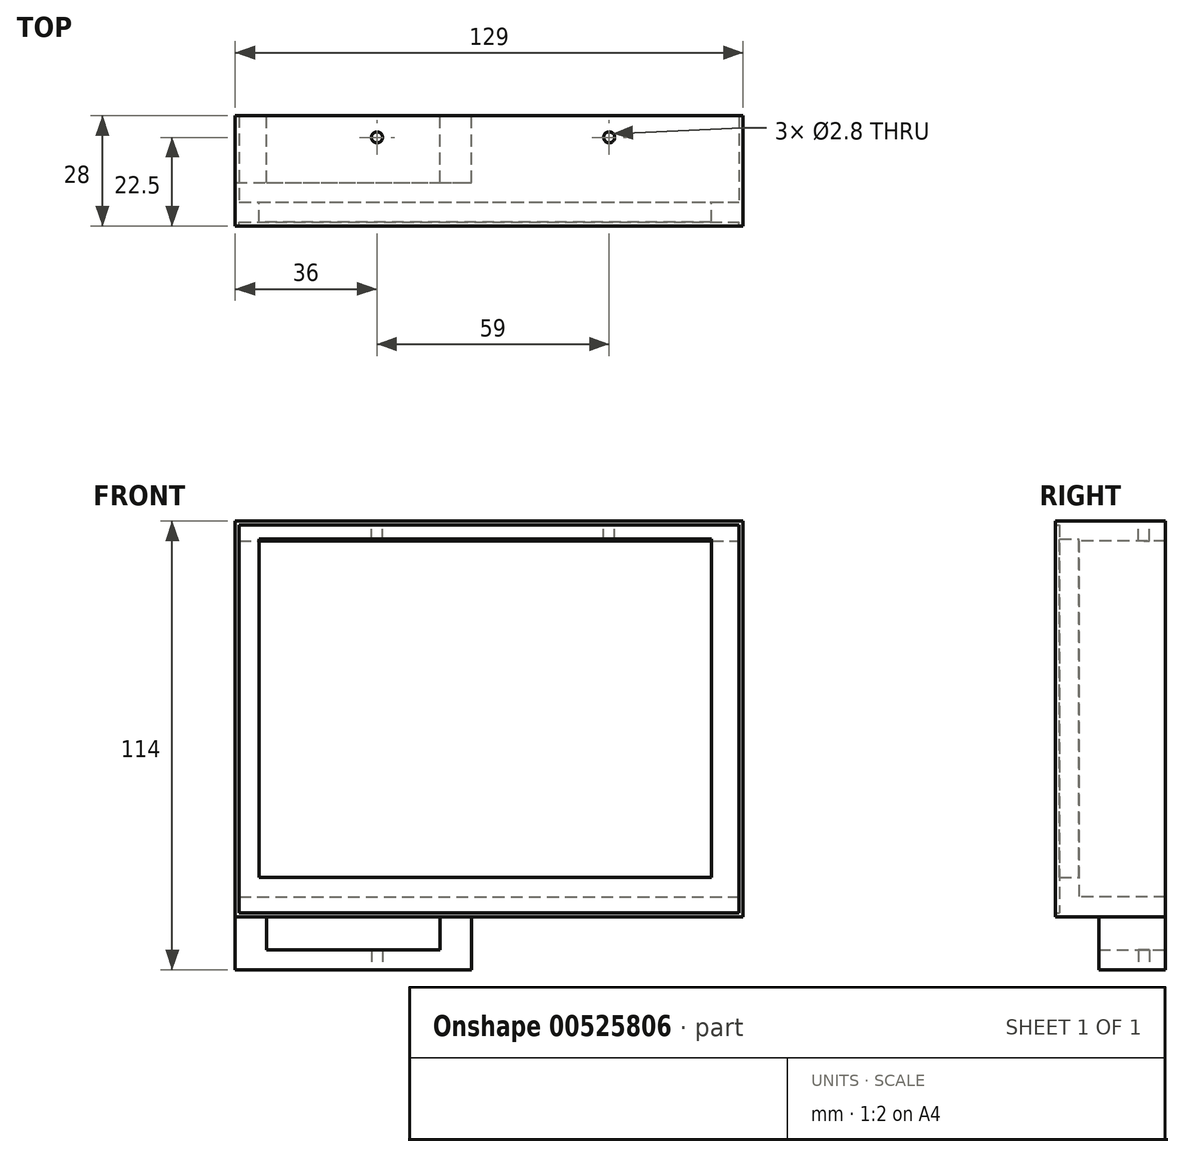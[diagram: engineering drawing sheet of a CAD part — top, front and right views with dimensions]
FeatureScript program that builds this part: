
annotation { "Feature Type Name" : "Feature", "Feature Type Description" : "" }
export const myFeature = defineFeature(function(context is Context, id is Id, definition is map)
    precondition{}
    {
        {
            var Q0;
            Q0=qCreatedBy(makeId("Front.planeOp"),FACE);
            var sketch = newSketch(context, id + "F0", { "sketchPlane" : qUnion([Q0])});
            skLineSegment(sketch, "E0.bottom", {"start": v(57.5, -43) * mm, "end": v(-57.5, -43) * mm});
            skLineSegment(sketch, "E0.top", {"start": v(57.5, 43) * mm, "end": v(-57.5, 43) * mm});
            skLineSegment(sketch, "E0.left", {"start": v(57.5, -43) * mm, "end": v(57.5, 43) * mm});
            skLineSegment(sketch, "E0.right", {"start": v(-57.5, -43) * mm, "end": v(-57.5, 43) * mm});
            skPoint(sketch, "E0.middle", {"position": v(0, 0) * mm});
            skLineSegment(sketch, "E1.bottom", {"start": v(-62.5, 46.5) * mm, "end": v(64.5, 46.5) * mm});
            skLineSegment(sketch, "E1.top", {"start": v(-62.5, -52) * mm, "end": v(64.5, -52) * mm});
            skLineSegment(sketch, "E1.left", {"start": v(-62.5, 46.5) * mm, "end": v(-62.5, -52) * mm});
            skLineSegment(sketch, "E1.right", {"start": v(64.5, 46.5) * mm, "end": v(64.5, -52) * mm});
            skSolve(sketch);
        }
        {
            var Q0;
            Q0=qCreatedBy(makeId("Front.planeOp"),FACE);
            var sketch = newSketch(context, id + "F1", { "sketchPlane" : qUnion([Q0])});
            skLineSegment(sketch, "E2.bottom", {"start": v(-62.5, 46.5) * mm, "end": v(64.5, 46.5) * mm});
            skLineSegment(sketch, "E2.top", {"start": v(-62.5, -52) * mm, "end": v(64.5, -52) * mm});
            skLineSegment(sketch, "E2.left", {"start": v(-62.5, 46.5) * mm, "end": v(-62.5, -52) * mm});
            skLineSegment(sketch, "E2.right", {"start": v(64.5, 46.5) * mm, "end": v(64.5, -52) * mm});
            skLineSegment(sketch, "E3.bottom", {"start": v(-63.5, 47.5) * mm, "end": v(65.5, 47.5) * mm});
            skLineSegment(sketch, "E3.top", {"start": v(-63.5, -53) * mm, "end": v(65.5, -53) * mm});
            skLineSegment(sketch, "E3.left", {"start": v(-63.5, 47.5) * mm, "end": v(-63.5, -53) * mm});
            skLineSegment(sketch, "E3.right", {"start": v(65.5, 47.5) * mm, "end": v(65.5, -53) * mm});
            skSolve(sketch);
        }
        {
            var Q0;
            Q0=qSketchRegion(id+"F1",true);
            extrude(context, id + "F2", {"entities" : qUnion([Q0]), "depth" : 6 * mm});
        }
        {
            var Q0;
            Q0=qCreatedBy(makeId("Front.planeOp"),FACE);
            var sketch = newSketch(context, id + "F3", { "sketchPlane" : qUnion([Q0])});
            skLineSegment(sketch, "E4.bottom", {"start": v(-63.5, 47.5) * mm, "end": v(65.5, 47.5) * mm});
            skLineSegment(sketch, "E4.top", {"start": v(-63.5, -53) * mm, "end": v(65.5, -53) * mm});
            skLineSegment(sketch, "E4.left", {"start": v(-63.5, 47.5) * mm, "end": v(-63.5, -53) * mm});
            skLineSegment(sketch, "E4.right", {"start": v(65.5, 47.5) * mm, "end": v(65.5, -53) * mm});
            skLineSegment(sketch, "E5.bottom", {"start": v(-62.5, 42.5) * mm, "end": v(64.5, 42.5) * mm});
            skLineSegment(sketch, "E5.top", {"start": v(-62.5, -48) * mm, "end": v(64.5, -48) * mm});
            skLineSegment(sketch, "E5.left", {"start": v(-62.5, 42.5) * mm, "end": v(-62.5, -48) * mm});
            skLineSegment(sketch, "E5.right", {"start": v(64.5, 42.5) * mm, "end": v(64.5, -48) * mm});
            skSolve(sketch);
        }
        {
            var Q0;
            Q0=qSketchRegion(id+"F3",true);
            extrude(context, id + "F4", {"entities" : qUnion([Q0]), "operationType" : NewBodyOperationType.ADD, "oppositeDirection" : true, "depth" : 22 * mm});
        }
        {
            var Q0;
            Q0=makeQuery(id+"F4.opExtrude","CAP_FACE",FACE,{"disambiguationData":[OSD([sQuery(id+"F3.wireOp",EDGE,"E4.bottom"),sQuery(id+"F3.wireOp",EDGE,"E4.top"),sQuery(id+"F3.wireOp",EDGE,"E4.left"),sQuery(id+"F3.wireOp",EDGE,"E4.right"),sQuery(id+"F3.wireOp",EDGE,"E5.bottom"),sQuery(id+"F3.wireOp",EDGE,"E5.top"),sQuery(id+"F3.wireOp",EDGE,"E5.left"),sQuery(id+"F3.wireOp",EDGE,"E5.right")])],"isStart":false});
            var sketch = newSketch(context, id + "F5", { "sketchPlane" : qUnion([Q0])});
            skLineSegment(sketch, "E6.top", {"start": v(63.5, -66.5) * mm, "end": v(3.5, -66.5) * mm});
            skLineSegment(sketch, "E6.left", {"start": v(63.5, -53) * mm, "end": v(63.5, -66.5) * mm});
            skLineSegment(sketch, "E6.right", {"start": v(3.5, -53) * mm, "end": v(3.5, -66.5) * mm});
            skLineSegment(sketch, "E7.top", {"start": v(55.5, -61.5) * mm, "end": v(11.5, -61.5) * mm});
            skLineSegment(sketch, "E7.left", {"start": v(55.5, -53) * mm, "end": v(55.5, -61.5) * mm});
            skLineSegment(sketch, "E7.right", {"start": v(11.5, -53) * mm, "end": v(11.5, -61.5) * mm});
            skLineSegment(sketch, "E8", {"start": v(63.5, -53) * mm, "end": v(55.5, -53) * mm});
            skLineSegment(sketch, "E9", {"start": v(11.5, -53) * mm, "end": v(3.5, -53) * mm});
            skSolve(sketch);
        }
        {
            var Q0;
            Q0=qSketchRegion(id+"F5",true);
            extrude(context, id + "F6", {"entities" : qUnion([Q0]), "operationType" : NewBodyOperationType.ADD, "oppositeDirection" : true, "depth" : 17 * mm});
        }
        {
            var Q0;
            Q0=makeQuery(id+"F4.boolean.opBoolean","MERGE",FACE,{"derivedFrom":[makeQuery(id+"F2.opExtrude","SWEPT_FACE",FACE,{"disambiguationData":[OSD([sQuery(id+"F1.wireOp",EDGE,"E3.bottom")])]}),makeQuery(id+"F4.opExtrude","SWEPT_FACE",FACE,{"disambiguationData":[OSD([sQuery(id+"F3.wireOp",EDGE,"E4.bottom")])]})]});
            var sketch = newSketch(context, id + "F7", { "sketchPlane" : qUnion([Q0])});
            skCircle(sketch, "E10", {"center": v(-27.5, 16.5) * mm, "radius": 1.4 * mm});
            skCircle(sketch, "E11", {"center": v(31.5, 16.5) * mm, "radius": 1.4 * mm});
            skSolve(sketch);
        }
        {
            var Q0;
            Q0=qSketchRegion(id+"F7",true);
            extrude(context, id + "F8", {"entities" : qUnion([Q0]), "operationType" : NewBodyOperationType.REMOVE, "oppositeDirection" : true, "depth" : 7.9 * mm});
        }
        {
            var Q0;
            Q0=makeQuery(id+"F6.opExtrude","SWEPT_FACE",FACE,{"disambiguationData":[OSD([sQuery(id+"F5.wireOp",EDGE,"E6.top")])]});
            var sketch = newSketch(context, id + "F9", { "sketchPlane" : qUnion([Q0])});
            skCircle(sketch, "E12", {"center": v(-27.5, -16.5) * mm, "radius": 1.4 * mm});
            skSolve(sketch);
        }
        {
            var Q0;
            Q0=qSketchRegion(id+"F9",true);
            extrude(context, id + "F10", {"entities" : qUnion([Q0]), "operationType" : NewBodyOperationType.REMOVE, "oppositeDirection" : true, "depth" : 5 * mm});
        }
        {
            var Q0;
            {var subQ0=sQuery(id+"F3.wireOp",EDGE,"E5.bottom");var subQ1=sQuery(id+"F3.wireOp",EDGE,"E5.left");var subQ2=sQuery(id+"F3.wireOp",EDGE,"E5.right");Q0=makeQuery(id+"F4.boolean.opBoolean","SPLIT",FACE,{"disambiguationData":[TD([makeQuery(id+"F2.opExtrude","SWEPT_FACE",FACE,{"disambiguationData":[OSD([sQuery(id+"F1.wireOp",EDGE,"E2.bottom")])]})])],"derivedFrom":makeQuery(id+"F4.opExtrude","CAP_FACE",FACE,{"disambiguationData":[OSD([sQuery(id+"F3.wireOp",EDGE,"E4.bottom"),sQuery(id+"F3.wireOp",EDGE,"E4.top"),sQuery(id+"F3.wireOp",EDGE,"E4.left"),sQuery(id+"F3.wireOp",EDGE,"E4.right"),subQ0,sQuery(id+"F3.wireOp",EDGE,"E5.top"),subQ1,subQ2])],"isStart":true})});}
            var sketch = newSketch(context, id + "F11", { "sketchPlane" : qUnion([Q0])});
            skLineSegment(sketch, "E13.bottom", {"start": v(57.5, -43) * mm, "end": v(-57.5, -43) * mm});
            skLineSegment(sketch, "E13.top", {"start": v(57.5, 43) * mm, "end": v(-57.5, 43) * mm});
            skLineSegment(sketch, "E13.left", {"start": v(57.5, -43) * mm, "end": v(57.5, 43) * mm});
            skLineSegment(sketch, "E13.right", {"start": v(-57.5, -43) * mm, "end": v(-57.5, 43) * mm});
            skPoint(sketch, "E13.middle", {"position": v(0, 0) * mm});
            skLineSegment(sketch, "E14.bottom", {"start": v(-62.5, 46.5) * mm, "end": v(64.5, 46.5) * mm});
            skLineSegment(sketch, "E14.top", {"start": v(-62.5, -52) * mm, "end": v(64.5, -52) * mm});
            skLineSegment(sketch, "E14.left", {"start": v(-62.5, 46.5) * mm, "end": v(-62.5, -52) * mm});
            skLineSegment(sketch, "E14.right", {"start": v(64.5, 46.5) * mm, "end": v(64.5, -52) * mm});
            skSolve(sketch);
        }
        {
            var Q0;
            Q0=qSketchRegion(id+"F11",true);
            extrude(context, id + "F12", {"entities" : qUnion([Q0]), "operationType" : NewBodyOperationType.ADD, "depth" : 5 * mm});
        }
    });
